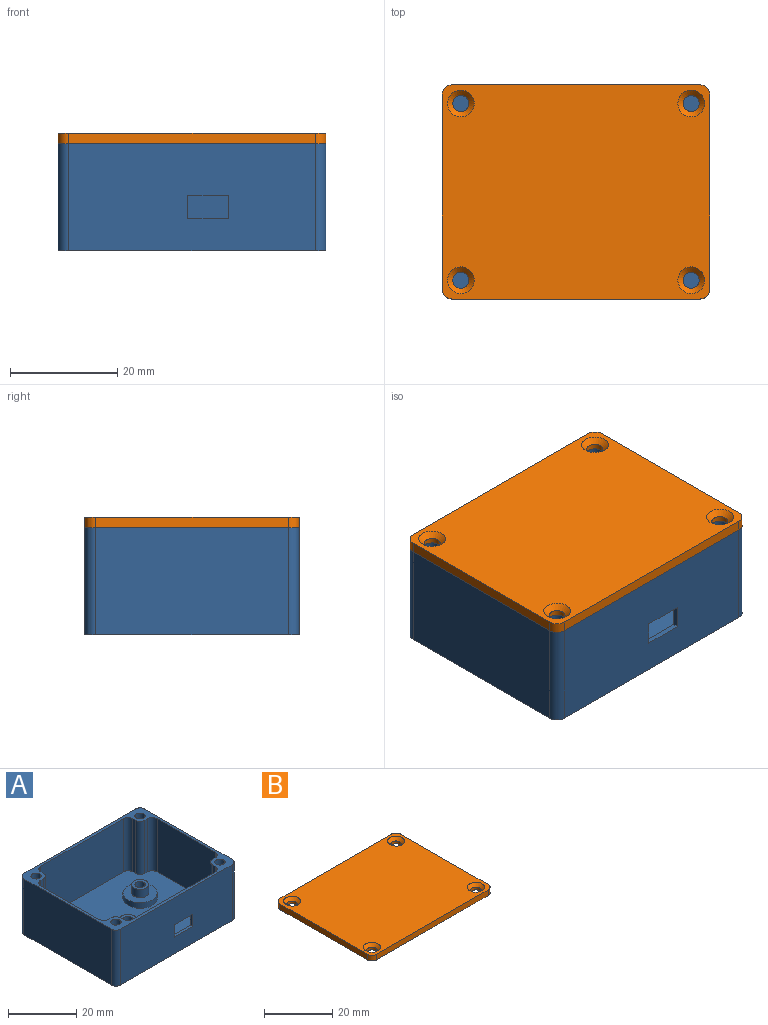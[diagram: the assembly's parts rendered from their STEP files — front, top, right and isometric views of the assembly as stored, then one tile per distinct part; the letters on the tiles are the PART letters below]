
ASSEMBLY  parts=2 mates=1
PART A: 71 faces, bbox 50x40x20 mm
  f0: plane 34x19mm, normal (0,1,0), area 613mm2, adj f4,f8,f55,f59,f67,f68,f69,f70
  f1: plane 46x20mm, normal (0,-1,0), area 887mm2, adj f8,f12,f52,f53,f67,f68,f69,f70
  f2: cylinder r=1.5mm len=4mm, axis (0,0,-1), area 37.7mm2, adj f30,f50
  f3: cylinder r=1.5mm len=4mm, axis (0,0,-1), area 37.7mm2, adj f32,f43
  f4: plane 48x38mm, normal (0,0,1), area 1563.5mm2, adj f0,f5,f6,f7,f13,f14,f15,f16
  f5: plane 24x19mm, normal (-1,0,0), area 456mm2, adj f4,f8,f57,f61
  f6: plane 34x19mm, normal (0,-1,0), area 646mm2, adj f4,f8,f62,f64
  f7: plane 24x19mm, normal (1,0,0), area 456mm2, adj f4,f8,f60,f66
  f8: plane 50x40mm, normal (0,0,1), area 247.7mm2, adj f0,f1,f5,f6,f7,f9,f10,f11
  f9: plane 46x20mm, normal (0,1,0), area 920mm2, adj f8,f12,f51,f54
  f10: plane 36x20mm, normal (-1,0,0), area 720mm2, adj f8,f12,f51,f52
  f11: plane 36x20mm, normal (1,0,0), area 720mm2, adj f8,f12,f53,f54
  f12: plane 50x40mm, normal (0,0,-1), area 1949.8mm2, adj f1,f9,f10,f11,f37,f38,f39,f40
  f13: plane 19x1mm, normal (0,-1,0), area 19mm2, adj f4,f8,f65,f66
  f14: plane 19x1mm, normal (1,0,0), area 19mm2, adj f4,f8,f64,f65
  f15: plane 19x1mm, normal (0,-1,0), area 19mm2, adj f4,f8,f61,f63
  f16: plane 19x1mm, normal (-1,0,0), area 19mm2, adj f4,f8,f62,f63
  f17: plane 19x1mm, normal (0,1,0), area 19mm2, adj f4,f8,f58,f60
  f18: plane 19x1mm, normal (1,0,0), area 19mm2, adj f4,f8,f58,f59
  f19: plane 19x1mm, normal (0,1,0), area 19mm2, adj f4,f8,f56,f57
  f20: plane 19x1mm, normal (-1,0,0), area 19mm2, adj f4,f8,f55,f56
  f21: cylinder r=1.5mm len=10mm, axis (0,0,1), area 94.2mm2, adj f8,f22
  f22: plane 3x3mm, normal (0,0,1), area 7.1mm2, adj f21
  f23: cylinder r=1.5mm len=10mm, axis (0,0,1), area 94.2mm2, adj f8,f24
  f24: plane 3x3mm, normal (0,0,1), area 7.1mm2, adj f23
  f25: cylinder r=1.5mm len=10mm, axis (0,0,1), area 94.2mm2, adj f8,f26
  f26: plane 3x3mm, normal (0,0,1), area 7.1mm2, adj f25
  f27: cylinder r=1.5mm len=10mm, axis (0,0,1), area 94.2mm2, adj f8,f28
  f28: plane 3x3mm, normal (0,0,1), area 7.1mm2, adj f27
  f29: cylinder r=2.5mm len=5mm, axis (0,0,-1), area 47.1mm2, adj f30,f34
  f30: plane 5x5mm, normal (0,0,1), area 12.6mm2, adj f2,f29
  f31: cylinder r=2.5mm len=5mm, axis (0,0,-1), area 47.1mm2, adj f32,f36
  f32: plane 5x5mm, normal (0,0,1), area 12.6mm2, adj f3,f31
  f33: cylinder r=5mm len=10mm, axis (0,0,-1), area 62.8mm2, adj f4,f34
  f34: plane 10x10mm, normal (0,0,1), area 58.9mm2, adj f29,f33
  f35: cylinder r=5mm len=10mm, axis (0,0,-1), area 62.8mm2, adj f4,f36
  f36: plane 10x10mm, normal (0,0,1), area 58.9mm2, adj f31,f35
  f37: plane 2.64x2mm, normal (0.88,-0.48,0), area 6mm2, adj f12,f38,f42,f43
  f38: plane 3x2mm, normal (0.03,-1,0), area 6mm2, adj f12,f37,f39,f43
  f39: plane 2.56x2mm, normal (-0.85,-0.52,0), area 6mm2, adj f12,f38,f40,f43
  f40: plane 2.64x2mm, normal (-0.88,0.48,0), area 6mm2, adj f12,f39,f41,f43
  f41: plane 3x2mm, normal (-0.03,1,0), area 6mm2, adj f12,f40,f42,f43
  f42: plane 2.56x2mm, normal (0.85,0.52,0), area 6mm2, adj f12,f37,f41,f43
  f43: plane 6x5.27mm, normal (0,0,-1), area 16.3mm2, adj f3,f37,f38,f39,f40,f41,f42
  f44: plane 2.97x2mm, normal (0.99,0.13,0), area 6mm2, adj f12,f45,f49,f50
  f45: plane 2.37x2mm, normal (0.61,-0.79,0), area 6mm2, adj f12,f44,f46,f50
  f46: plane 2.78x2mm, normal (-0.38,-0.93,0), area 6mm2, adj f12,f45,f47,f50
  f47: plane 2.97x2mm, normal (-0.99,-0.13,0), area 6mm2, adj f12,f46,f48,f50
  f48: plane 2.37x2mm, normal (-0.61,0.79,0), area 6mm2, adj f12,f47,f49,f50
  f49: plane 2.78x2mm, normal (0.38,0.93,0), area 6mm2, adj f12,f44,f48,f50
  f50: plane 5.95x5.55mm, normal (0,0,-1), area 16.3mm2, adj f2,f44,f45,f46,f47,f48,f49
  f51: cylinder r=2mm len=20mm, axis (0,0,1), area 62.8mm2, adj f8,f9,f10,f12
  f52: cylinder r=2mm len=20mm, axis (0,0,-1), area 62.8mm2, adj f1,f8,f10,f12
  f53: cylinder r=2mm len=20mm, axis (0,0,1), area 62.8mm2, adj f1,f8,f11,f12
  f54: cylinder r=2mm len=20mm, axis (0,0,-1), area 62.8mm2, adj f8,f9,f11,f12
  f55: cylinder r=2mm len=19mm, axis (0,0,-1), area 59.7mm2, adj f0,f4,f8,f20
  f56: cylinder r=2mm len=19mm, axis (0,0,1), area 59.7mm2, adj f4,f8,f19,f20
  f57: cylinder r=2mm len=19mm, axis (0,0,-1), area 59.7mm2, adj f4,f5,f8,f19
  f58: cylinder r=2mm len=19mm, axis (0,0,1), area 59.7mm2, adj f4,f8,f17,f18
  f59: cylinder r=2mm len=19mm, axis (0,0,1), area 59.7mm2, adj f0,f4,f8,f18
  f60: cylinder r=2mm len=19mm, axis (0,0,-1), area 59.7mm2, adj f4,f7,f8,f17
  f61: cylinder r=2mm len=19mm, axis (0,0,1), area 59.7mm2, adj f4,f5,f8,f15
  f62: cylinder r=2mm len=19mm, axis (0,0,-1), area 59.7mm2, adj f4,f6,f8,f16
  f63: cylinder r=2mm len=19mm, axis (0,0,1), area 59.7mm2, adj f4,f8,f15,f16
  f64: cylinder r=2mm len=19mm, axis (0,0,1), area 59.7mm2, adj f4,f6,f8,f14
  f65: cylinder r=2mm len=19mm, axis (0,0,1), area 59.7mm2, adj f4,f8,f13,f14
  f66: cylinder r=2mm len=19mm, axis (0,0,1), area 59.7mm2, adj f4,f7,f8,f13
  f67: plane 7.54x1mm, normal (0,0,-1), area 7.5mm2, adj f0,f1,f68,f70
  f68: plane 4.38x1mm, normal (1,0,0), area 4.4mm2, adj f0,f1,f67,f69
  f69: plane 7.54x1mm, normal (0,0,1), area 7.5mm2, adj f0,f1,f68,f70
  f70: plane 4.38x1mm, normal (-1,0,0), area 4.4mm2, adj f0,f1,f67,f69
PART B: 18 faces, bbox 50x40x2 mm
  f0: plane 36x2mm, normal (-1,0,0), area 72mm2, adj f4,f5,f14,f17
  f1: plane 46x2mm, normal (0,-1,0), area 92mm2, adj f4,f5,f14,f15
  f2: plane 36x2mm, normal (1,0,0), area 72mm2, adj f4,f5,f15,f16
  f3: plane 46x2mm, normal (0,1,0), area 92mm2, adj f4,f5,f16,f17
  f4: plane 50x40mm, normal (0,0,1), area 1918mm2, adj f0,f1,f2,f3,f10,f11,f12,f13
  f5: plane 50x40mm, normal (0,0,-1), area 1968.3mm2, adj f0,f1,f2,f3,f6,f7,f8,f9
  f6: cylinder r=1.5mm len=3mm, axis (0,0,1), area 9.4mm2, adj f5,f13
  f7: cylinder r=1.5mm len=3mm, axis (0,0,1), area 9.4mm2, adj f5,f11
  f8: cylinder r=1.5mm len=3mm, axis (0,0,1), area 9.4mm2, adj f5,f10
  f9: cylinder r=1.5mm len=3mm, axis (0,0,1), area 9.4mm2, adj f5,f12
  f10: cone r=1.5mm half-angle=45deg, axis (0,0,1), area 17.8mm2, adj f4,f8
  f11: cone r=1.5mm half-angle=45deg, axis (0,0,1), area 17.8mm2, adj f4,f7
  f12: cone r=1.5mm half-angle=45deg, axis (0,0,1), area 17.8mm2, adj f4,f9
  f13: cone r=1.5mm half-angle=45deg, axis (0,0,1), area 17.8mm2, adj f4,f6
  f14: cylinder r=2mm len=2mm, axis (0,0,1), area 6.3mm2, adj f0,f1,f4,f5
  f15: cylinder r=2mm len=2mm, axis (0,0,-1), area 6.3mm2, adj f1,f2,f4,f5
  f16: cylinder r=2mm len=2mm, axis (0,0,1), area 6.3mm2, adj f2,f3,f4,f5
  f17: cylinder r=2mm len=2mm, axis (0,0,-1), area 6.3mm2, adj f0,f3,f4,f5
PLACE A t=(-42.16,-25.55,24.98)mm fixed
PLACE B t=(-127.59,-29.04,44.98)mm
MATE slider A.f23 <-> B.f8  axis (0,0,1) through (-61.93,-1.52,44.98)mm
